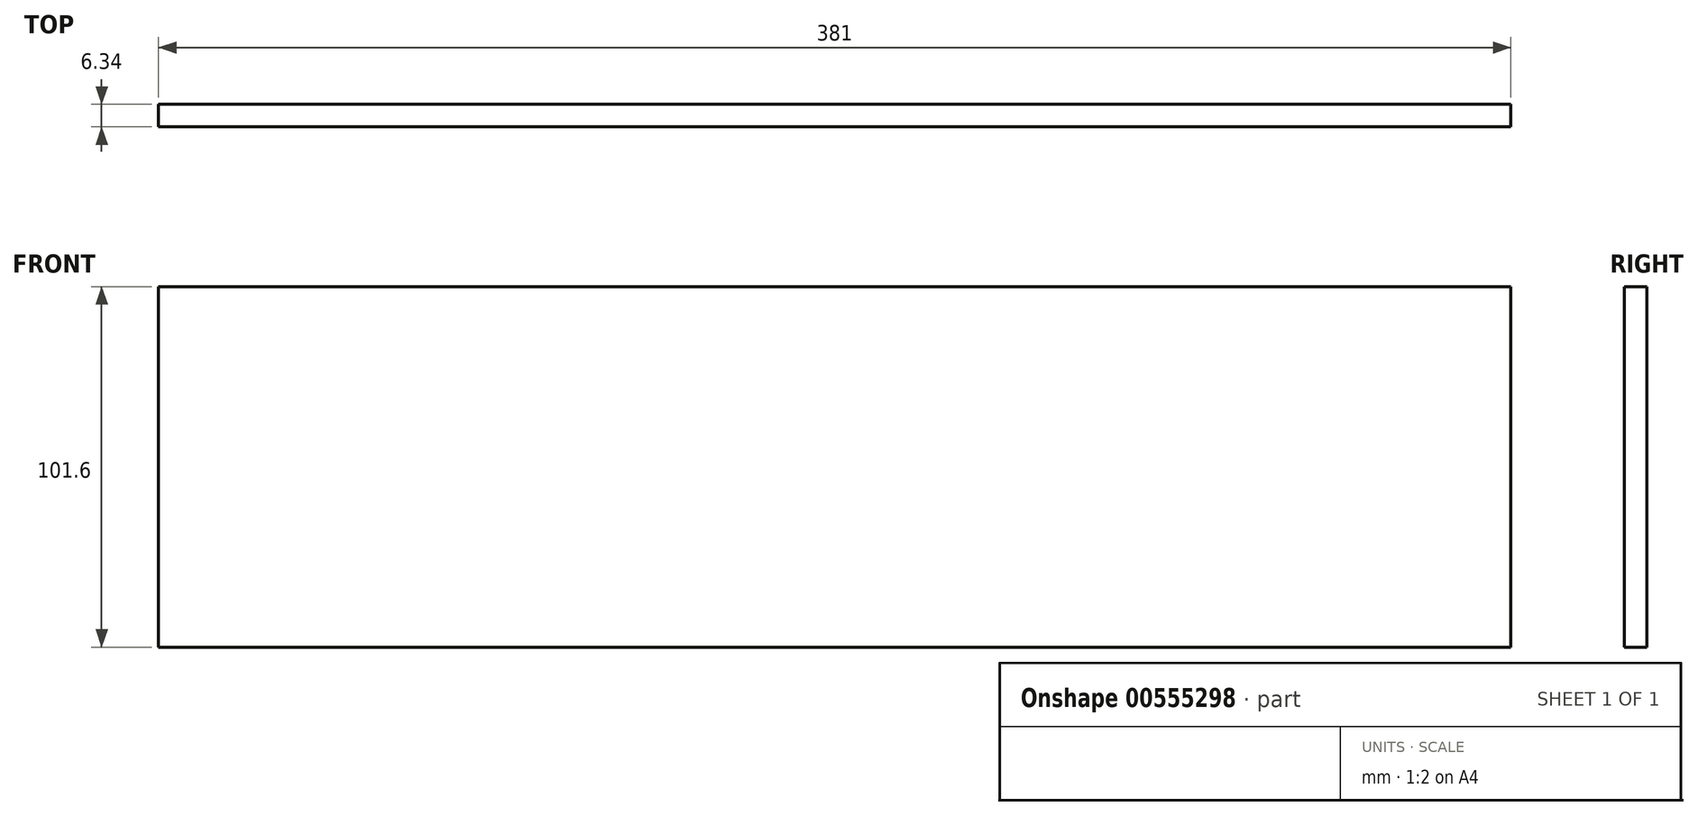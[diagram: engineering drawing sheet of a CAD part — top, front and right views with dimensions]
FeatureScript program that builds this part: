
annotation { "Feature Type Name" : "Feature", "Feature Type Description" : "" }
export const myFeature = defineFeature(function(context is Context, id is Id, definition is map)
    precondition{}
    {
        {
            var Q0;
            Q0=qCreatedBy(makeId("Front.planeOp"),FACE);
            var sketch = newSketch(context, id + "F0", { "sketchPlane" : qUnion([Q0])});
            skLineSegment(sketch, "E0.bottom", {"start": v(-190.5, 50.8) * mm, "end": v(190.5, 50.8) * mm});
            skLineSegment(sketch, "E0.top", {"start": v(-190.5, -50.8) * mm, "end": v(190.5, -50.8) * mm});
            skLineSegment(sketch, "E0.left", {"start": v(-190.5, 50.8) * mm, "end": v(-190.5, -50.8) * mm});
            skLineSegment(sketch, "E0.right", {"start": v(190.5, 50.8) * mm, "end": v(190.5, -50.8) * mm});
            skPoint(sketch, "E0.middle", {"position": v(0, 0) * mm});
            skSolve(sketch);
        }
        {
            var Q0;
            Q0=makeQuery(id+"F0.imprint","IMPRINT",FACE,{"disambiguationData":[TD([[makeQuery(id+"F0.imprint","IMPRINT",EDGE,{"derivedFrom":sQuery(id+"F0.wireOp",EDGE,"E0.bottom")}),-1.0]])]});
            extrude(context, id + "F1", {"entities" : qUnion([Q0]), "endBound" : BoundingType.SYMMETRIC, "depth" : 6.35 * mm, "offsetDistance" : 25.4 * mm});
        }
    });
